# Revit family: rba-bim-rba1044 Series
name_source: partatom
category: Plumbing Fixtures
revit_build: Autodesk Revit 2018 (Build: 20170223_1515(x64)
units: mm (PartAtom-declared; Revit-internal decimal feet)

## family parameters
Always vertical = Yes
Cut with Voids When Loaded = No
Part Type = Normal
Room Calculation Point = No
Round Connector Dimension = Use Diameter
Shared = No
Work Plane-Based = Yes

## types (4) — shared parameters
Default Elevation = 1219.2 mm  [stored 4 ft]
Manufacturer = RBA Group
Materials and Finishes = Polished Chrome Finish

## per-type parameters (varying)
| type | Description | Modified Issue | URL |
| RBA1044-600 | ‘Rio’ Water Saving Tap, 6 Star WELS, 5L pm | 20220328.01 | www.rba.com.au |
| RBA1044-400 | 4 Star WELS, 8L pm |  | www.rba.com.au/tapware/basin-mounted |
| RBA1043-600 | 6 Star WELS, 5L pm |  | www.rba.com.au |
| RBA1043-400 | 4 Star WELS |  | www.rba.com.au |

note: column(s) folded — value = type name in every type: Model

note: [stored X ft] marks values corroborated as IEEE doubles in the binary element streams (Revit-internal decimal feet)

## geometry (parser evidence)
native form markers: Blend x2, Sweep x3
no freeform markers — native parametric forms only
